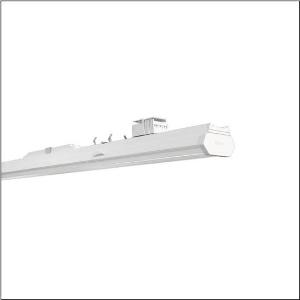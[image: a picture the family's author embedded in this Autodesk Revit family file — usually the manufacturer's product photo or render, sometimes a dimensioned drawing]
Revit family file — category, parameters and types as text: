
# Revit family: licross_r__21_protected_ho_52td13mn4fxs_5700
name_source: partatom
category: Lighting Fixtures
units: mm (PartAtom-declared; Revit-internal decimal feet)

## family parameters
Cut with Voids When Loaded = No
Host = Face
Light Source = No
Part Type = Normal
Room Calculation Point = No
Round Connector Dimension = Use Diameter
Shared = No

## types (1)
- --- (1 x LED, 15060 lm, 83.2 W, 4000K)
    Apparent Load = 83 VA
    CIE Flux Codes = 89 96 99 100 99
    Color Rendering = 80
    Color Temperature = 4000K
    Default Elevation = 1800 mm
    Description = Licross® 21 Protected HO, luminaire insert, of sheet steel, galvanised, coil coated, white, length: 1.500mm, width: 66mm, height: 67mm, LED rated luminous flux: 15.060lm, light colour: 840, control gear: ON/OFF Multilumen, with plug, 3-pole, with phase selection, mains connection: 220..240V, AC, 50/60Hz, rated input power: 83W, halogen-free wiring, primary light control with lens, of plastic, primary optical cover: cover, of PMMA, light emission: direct distribution, primary light characteristic: symmetric, protection rating (complete): IP54, insulation class (complete): insulation class I (protective earthing), certification: CE, ENEC, VDE, UKCA, protection symbol: D if used in an environment with non-conductive dust loads with corresponding accessories, impact resistance: IK06, permissible ambient temperature for indoor applications: -35..+35°C, corresponds to IFS (International Featured Standards) requirements for safety and quality in the food industry, reducing of maximum allowable ambient temperature of 5°C with ceiling mounting, LABS conformity tested according to VDMA 24364:2018-05, packaging unit: 1 piece
    Height = 92 mm
    Lamp = 1 x LED
    Lamp Light Flux = 15060 lm
    Lamp Power = 83.2 W
    Lamp count = 1
    Length = 1500 mm
    Luminous efficacy = 181 lm/W
    Manufacturer = Siteco
    ModVariant = No
    Model = 52TD13MN4FXS
    Mounting Place = Ceiling
    Mounting Type = Pendant
    Number of Poles = 1
    OnlyDefault = Yes
    Power Factor = 1
    Product Name = Licross® 21 Protected HO
    Product group = luminaire insert
    ProductGroupID = 901
    Protection Class = Protection class I
    Protection Degree = IP 54
    RLX_Detail_Level = 1
    RLX_Emergency_Light_Flux = 0 lm
    RLX_Emergency_Type = 0
    RLX_Emergency_Type_DB = No
    RlxData = <blob elided: 22005 chars, md5=6d4d86c6>
    Socket = socket
    Standby Power = 0 W
    System Light Flux = 15060 lm
    System Power = 83 W
    Type Comments = factory setting: luminous flux: 100 % | (A | C | E) | 195 mA
    Type Image = l_1256148.jpg
    URL = http://relux.com
    VarID = @adj_039173
    Voltage = 0 V
    Weight = 0.00 kg
    Width = 88 mm

## geometry (parser evidence)
native form markers: Blend x4, Sweep x10
no freeform markers — native parametric forms only
